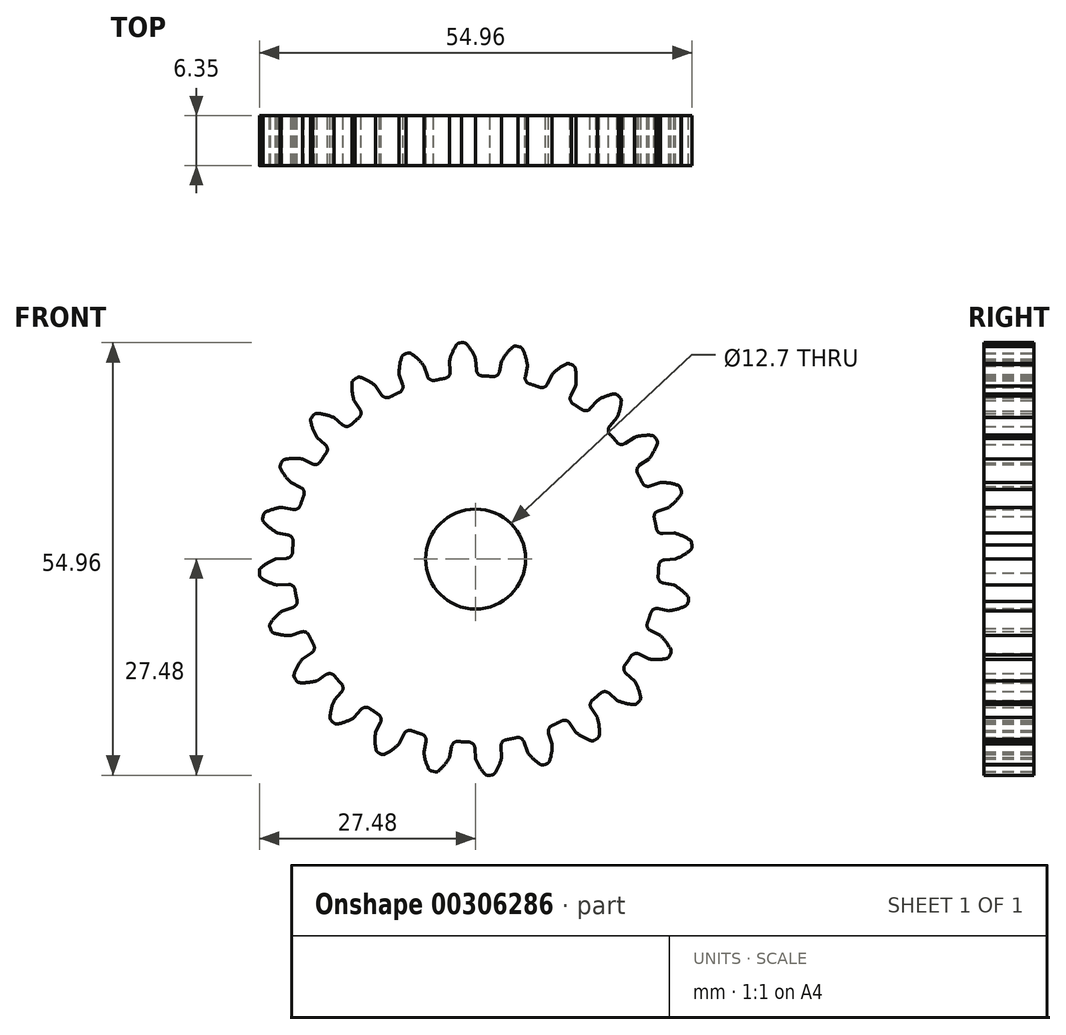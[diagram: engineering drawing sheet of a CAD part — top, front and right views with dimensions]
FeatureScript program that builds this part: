
annotation { "Feature Type Name" : "Feature", "Feature Type Description" : "" }
export const myFeature = defineFeature(function(context is Context, id is Id, definition is map)
    precondition{}
    {
        {
            var Q0;
            Q0=qCreatedBy(makeId("Front.planeOp"),FACE);
            var sketch = newSketch(context, id + "F0", { "sketchPlane" : qUnion([Q0])});
            skArc(sketch, "E0", {"start": v(-3.89, 22.95) * mm, "mid": v(1.52, -23.23) * mm, "end": v(0.86, 23.26) * mm});
            skArc(sketch, "E1.trimOffspring", {"start": v(0, 25.4) * mm, "mid": v(-0.5, 26.4) * mm, "end": v(-1.15, 27.3) * mm});
            skLineSegment(sketch, "E2", {"start": v(0, 25.4) * mm, "end": v(0.1, 24.01) * mm});
            skLineSegment(sketch, "E3", {"start": v(-1.53, 27.48) * mm, "end": v(-1.8, 27.48) * mm});
            skLineSegment(sketch, "E4.MirrorCS", {"start": v(-2.07, 27.44) * mm, "end": v(-1.8, 27.48) * mm});
            skArc(sketch, "E5.MirrorCS", {"start": v(-3.32, 25.18) * mm, "mid": v(-2.96, 26.24) * mm, "end": v(-2.42, 27.22) * mm});
            skLineSegment(sketch, "E6.MirrorCS", {"start": v(-3.32, 25.18) * mm, "end": v(-3.22, 23.8) * mm});
            skPoint(sketch, "E7.visualSharp", {"position": v(-1.3, 27.48) * mm});
            skArc(sketch, "E7.filletArc", {"start": v(-1.15, 27.3) * mm, "mid": v(-1.32, 27.43) * mm, "end": v(-1.53, 27.48) * mm});
            skPoint(sketch, "E8.visualSharp", {"position": v(-2.3, 27.41) * mm});
            skArc(sketch, "E8.filletArc", {"start": v(-2.07, 27.44) * mm, "mid": v(-2.27, 27.37) * mm, "end": v(-2.42, 27.22) * mm});
            skPoint(sketch, "E9.visualSharp", {"position": v(0.14, 23.28) * mm});
            skArc(sketch, "E9.filletArc", {"start": v(0.1, 24.01) * mm, "mid": v(0.33, 23.49) * mm, "end": v(0.86, 23.26) * mm});
            skPoint(sketch, "E10.visualSharp", {"position": v(-3.18, 23.06) * mm});
            skArc(sketch, "E10.filletArc", {"start": v(-3.89, 22.95) * mm, "mid": v(-3.4, 23.24) * mm, "end": v(-3.22, 23.8) * mm});
            skLineSegment(sketch, "E11.1.0", {"start": v(-9.72, 23.47) * mm, "end": v(-9.27, 22.15) * mm});
            skLineSegment(sketch, "E11.1.1", {"start": v(-6.57, 24.53) * mm, "end": v(-6.13, 23.22) * mm});
            skPoint(sketch, "E11.1.2", {"position": v(-8.37, 26.2) * mm});
            skArc(sketch, "E11.1.3", {"start": v(-6.13, 23.22) * mm, "mid": v(-5.76, 22.77) * mm, "end": v(-5.2, 22.7) * mm});
            skArc(sketch, "E11.1.4", {"start": v(-6.57, 24.53) * mm, "mid": v(-7.3, 25.38) * mm, "end": v(-8.18, 26.08) * mm});
            skPoint(sketch, "E11.1.5", {"position": v(-9.3, 25.89) * mm});
            skArc(sketch, "E11.1.6", {"start": v(-9.72, 23.47) * mm, "mid": v(-9.65, 24.58) * mm, "end": v(-9.39, 25.67) * mm});
            skArc(sketch, "E11.1.7", {"start": v(-9.7, 21.16) * mm, "mid": v(-9.3, 21.57) * mm, "end": v(-9.27, 22.15) * mm});
            skLineSegment(sketch, "E11.1.8", {"start": v(-8.6, 26.14) * mm, "end": v(-8.85, 26.07) * mm});
            skArc(sketch, "E11.1.9", {"start": v(-8.18, 26.08) * mm, "mid": v(-8.38, 26.15) * mm, "end": v(-8.6, 26.14) * mm});
            skArc(sketch, "E11.1.10", {"start": v(-9.1, 25.97) * mm, "mid": v(-9.28, 25.85) * mm, "end": v(-9.39, 25.67) * mm});
            skLineSegment(sketch, "E11.1.11", {"start": v(-9.1, 25.97) * mm, "end": v(-8.85, 26.07) * mm});
            skLineSegment(sketch, "E11.2.0", {"start": v(-15.46, 20.15) * mm, "end": v(-14.69, 19) * mm});
            skLineSegment(sketch, "E11.2.1", {"start": v(-12.7, 22) * mm, "end": v(-11.93, 20.84) * mm});
            skPoint(sketch, "E11.2.2", {"position": v(-14.87, 23.14) * mm});
            skArc(sketch, "E11.2.3", {"start": v(-11.93, 20.84) * mm, "mid": v(-11.46, 20.5) * mm, "end": v(-10.89, 20.58) * mm});
            skArc(sketch, "E11.2.4", {"start": v(-12.7, 22) * mm, "mid": v(-13.63, 22.62) * mm, "end": v(-14.65, 23.07) * mm});
            skPoint(sketch, "E11.2.5", {"position": v(-15.7, 22.6) * mm});
            skArc(sketch, "E11.2.6", {"start": v(-15.46, 20.15) * mm, "mid": v(-15.68, 21.25) * mm, "end": v(-15.7, 22.36) * mm});
            skArc(sketch, "E11.2.7", {"start": v(-14.84, 17.93) * mm, "mid": v(-14.56, 18.43) * mm, "end": v(-14.69, 19) * mm});
            skLineSegment(sketch, "E11.2.8", {"start": v(-15.06, 23.03) * mm, "end": v(-15.3, 22.9) * mm});
            skArc(sketch, "E11.2.9", {"start": v(-14.65, 23.07) * mm, "mid": v(-14.86, 23.1) * mm, "end": v(-15.06, 23.03) * mm});
            skArc(sketch, "E11.2.10", {"start": v(-15.51, 22.73) * mm, "mid": v(-15.65, 22.57) * mm, "end": v(-15.7, 22.36) * mm});
            skLineSegment(sketch, "E11.2.11", {"start": v(-15.51, 22.73) * mm, "end": v(-15.3, 22.9) * mm});
            skLineSegment(sketch, "E11.3.0", {"start": v(-20.15, 15.46) * mm, "end": v(-19.1, 14.54) * mm});
            skLineSegment(sketch, "E11.3.1", {"start": v(-17.96, 17.96) * mm, "end": v(-16.91, 17.04) * mm});
            skPoint(sketch, "E11.3.2", {"position": v(-20.35, 18.5) * mm});
            skArc(sketch, "E11.3.3", {"start": v(-16.91, 17.04) * mm, "mid": v(-16.37, 16.84) * mm, "end": v(-15.84, 17.06) * mm});
            skArc(sketch, "E11.3.4", {"start": v(-17.96, 17.96) * mm, "mid": v(-19.02, 18.32) * mm, "end": v(-20.12, 18.5) * mm});
            skPoint(sketch, "E11.3.5", {"position": v(-21, 17.76) * mm});
            skArc(sketch, "E11.3.6", {"start": v(-20.15, 15.46) * mm, "mid": v(-20.65, 16.46) * mm, "end": v(-20.96, 17.53) * mm});
            skArc(sketch, "E11.3.7", {"start": v(-18.98, 13.48) * mm, "mid": v(-18.84, 14.04) * mm, "end": v(-19.1, 14.54) * mm});
            skLineSegment(sketch, "E11.3.8", {"start": v(-20.51, 18.35) * mm, "end": v(-20.7, 18.16) * mm});
            skArc(sketch, "E11.3.9", {"start": v(-20.12, 18.5) * mm, "mid": v(-20.33, 18.46) * mm, "end": v(-20.51, 18.35) * mm});
            skArc(sketch, "E11.3.10", {"start": v(-20.87, 17.94) * mm, "mid": v(-20.96, 17.75) * mm, "end": v(-20.96, 17.53) * mm});
            skLineSegment(sketch, "E11.3.11", {"start": v(-20.87, 17.94) * mm, "end": v(-20.7, 18.16) * mm});
            skLineSegment(sketch, "E11.4.0", {"start": v(-23.47, 9.72) * mm, "end": v(-22.22, 9.1) * mm});
            skLineSegment(sketch, "E11.4.1", {"start": v(-22, 12.7) * mm, "end": v(-20.75, 12.08) * mm});
            skPoint(sketch, "E11.4.2", {"position": v(-24.45, 12.6) * mm});
            skArc(sketch, "E11.4.3", {"start": v(-20.75, 12.08) * mm, "mid": v(-20.18, 12.03) * mm, "end": v(-19.72, 12.38) * mm});
            skArc(sketch, "E11.4.4", {"start": v(-22, 12.7) * mm, "mid": v(-23.11, 12.78) * mm, "end": v(-24.22, 12.66) * mm});
            skPoint(sketch, "E11.4.5", {"position": v(-24.89, 11.72) * mm});
            skArc(sketch, "E11.4.6", {"start": v(-23.47, 9.72) * mm, "mid": v(-24.2, 10.56) * mm, "end": v(-24.79, 11.51) * mm});
            skArc(sketch, "E11.4.7", {"start": v(-21.82, 8.1) * mm, "mid": v(-21.83, 8.68) * mm, "end": v(-22.22, 9.1) * mm});
            skLineSegment(sketch, "E11.4.8", {"start": v(-24.56, 12.41) * mm, "end": v(-24.7, 12.18) * mm});
            skArc(sketch, "E11.4.9", {"start": v(-24.22, 12.66) * mm, "mid": v(-24.42, 12.57) * mm, "end": v(-24.56, 12.41) * mm});
            skArc(sketch, "E11.4.10", {"start": v(-24.8, 11.93) * mm, "mid": v(-24.84, 11.72) * mm, "end": v(-24.79, 11.51) * mm});
            skLineSegment(sketch, "E11.4.11", {"start": v(-24.8, 11.93) * mm, "end": v(-24.7, 12.18) * mm});
            skLineSegment(sketch, "E11.5.0", {"start": v(-25.18, 3.32) * mm, "end": v(-23.82, 3.04) * mm});
            skLineSegment(sketch, "E11.5.1", {"start": v(-24.53, 6.57) * mm, "end": v(-23.17, 6.3) * mm});
            skPoint(sketch, "E11.5.2", {"position": v(-26.88, 5.85) * mm});
            skArc(sketch, "E11.5.3", {"start": v(-23.17, 6.3) * mm, "mid": v(-22.6, 6.4) * mm, "end": v(-22.25, 6.85) * mm});
            skArc(sketch, "E11.5.4", {"start": v(-24.53, 6.57) * mm, "mid": v(-25.63, 6.36) * mm, "end": v(-26.67, 5.96) * mm});
            skPoint(sketch, "E11.5.5", {"position": v(-27.07, 4.88) * mm});
            skArc(sketch, "E11.5.6", {"start": v(-25.18, 3.32) * mm, "mid": v(-26.11, 3.93) * mm, "end": v(-26.92, 4.7) * mm});
            skArc(sketch, "E11.5.7", {"start": v(-23.18, 2.18) * mm, "mid": v(-23.33, 2.74) * mm, "end": v(-23.82, 3.04) * mm});
            skLineSegment(sketch, "E11.5.8", {"start": v(-26.94, 5.63) * mm, "end": v(-27, 5.37) * mm});
            skArc(sketch, "E11.5.9", {"start": v(-26.67, 5.96) * mm, "mid": v(-26.84, 5.82) * mm, "end": v(-26.94, 5.63) * mm});
            skArc(sketch, "E11.5.10", {"start": v(-27.04, 5.1) * mm, "mid": v(-27.02, 4.9) * mm, "end": v(-26.92, 4.7) * mm});
            skLineSegment(sketch, "E11.5.11", {"start": v(-27.04, 5.1) * mm, "end": v(-27, 5.37) * mm});
            skLineSegment(sketch, "E11.6.0", {"start": v(-25.18, -3.32) * mm, "end": v(-23.8, -3.22) * mm});
            skLineSegment(sketch, "E11.6.1", {"start": v(-25.4, 0) * mm, "end": v(-24.01, 0.1) * mm});
            skPoint(sketch, "E11.6.2", {"position": v(-27.48, -1.3) * mm});
            skArc(sketch, "E11.6.3", {"start": v(-24.01, 0.1) * mm, "mid": v(-23.49, 0.33) * mm, "end": v(-23.26, 0.86) * mm});
            skArc(sketch, "E11.6.4", {"start": v(-25.4, 0) * mm, "mid": v(-26.4, -0.5) * mm, "end": v(-27.3, -1.15) * mm});
            skPoint(sketch, "E11.6.5", {"position": v(-27.41, -2.3) * mm});
            skArc(sketch, "E11.6.6", {"start": v(-25.18, -3.32) * mm, "mid": v(-26.24, -2.96) * mm, "end": v(-27.22, -2.42) * mm});
            skArc(sketch, "E11.6.7", {"start": v(-22.95, -3.89) * mm, "mid": v(-23.24, -3.4) * mm, "end": v(-23.8, -3.22) * mm});
            skLineSegment(sketch, "E11.6.8", {"start": v(-27.48, -1.53) * mm, "end": v(-27.48, -1.8) * mm});
            skArc(sketch, "E11.6.9", {"start": v(-27.3, -1.15) * mm, "mid": v(-27.43, -1.32) * mm, "end": v(-27.48, -1.53) * mm});
            skArc(sketch, "E11.6.10", {"start": v(-27.44, -2.07) * mm, "mid": v(-27.37, -2.27) * mm, "end": v(-27.22, -2.42) * mm});
            skLineSegment(sketch, "E11.6.11", {"start": v(-27.44, -2.07) * mm, "end": v(-27.48, -1.8) * mm});
            skLineSegment(sketch, "E11.7.0", {"start": v(-23.47, -9.72) * mm, "end": v(-22.15, -9.27) * mm});
            skLineSegment(sketch, "E11.7.1", {"start": v(-24.53, -6.57) * mm, "end": v(-23.22, -6.13) * mm});
            skPoint(sketch, "E11.7.2", {"position": v(-26.2, -8.37) * mm});
            skArc(sketch, "E11.7.3", {"start": v(-23.22, -6.13) * mm, "mid": v(-22.77, -5.76) * mm, "end": v(-22.7, -5.2) * mm});
            skArc(sketch, "E11.7.4", {"start": v(-24.53, -6.57) * mm, "mid": v(-25.38, -7.3) * mm, "end": v(-26.08, -8.18) * mm});
            skPoint(sketch, "E11.7.5", {"position": v(-25.89, -9.3) * mm});
            skArc(sketch, "E11.7.6", {"start": v(-23.47, -9.72) * mm, "mid": v(-24.58, -9.65) * mm, "end": v(-25.67, -9.39) * mm});
            skArc(sketch, "E11.7.7", {"start": v(-21.16, -9.7) * mm, "mid": v(-21.57, -9.3) * mm, "end": v(-22.15, -9.27) * mm});
            skLineSegment(sketch, "E11.7.8", {"start": v(-26.14, -8.6) * mm, "end": v(-26.07, -8.85) * mm});
            skArc(sketch, "E11.7.9", {"start": v(-26.08, -8.18) * mm, "mid": v(-26.15, -8.38) * mm, "end": v(-26.14, -8.6) * mm});
            skArc(sketch, "E11.7.10", {"start": v(-25.97, -9.1) * mm, "mid": v(-25.85, -9.28) * mm, "end": v(-25.67, -9.39) * mm});
            skLineSegment(sketch, "E11.7.11", {"start": v(-25.97, -9.1) * mm, "end": v(-26.07, -8.85) * mm});
            skLineSegment(sketch, "E11.8.0", {"start": v(-20.15, -15.46) * mm, "end": v(-19, -14.69) * mm});
            skLineSegment(sketch, "E11.8.1", {"start": v(-22, -12.7) * mm, "end": v(-20.84, -11.93) * mm});
            skPoint(sketch, "E11.8.2", {"position": v(-23.14, -14.87) * mm});
            skArc(sketch, "E11.8.3", {"start": v(-20.84, -11.93) * mm, "mid": v(-20.5, -11.46) * mm, "end": v(-20.58, -10.89) * mm});
            skArc(sketch, "E11.8.4", {"start": v(-22, -12.7) * mm, "mid": v(-22.62, -13.63) * mm, "end": v(-23.07, -14.65) * mm});
            skPoint(sketch, "E11.8.5", {"position": v(-22.6, -15.7) * mm});
            skArc(sketch, "E11.8.6", {"start": v(-20.15, -15.46) * mm, "mid": v(-21.25, -15.68) * mm, "end": v(-22.36, -15.7) * mm});
            skArc(sketch, "E11.8.7", {"start": v(-17.93, -14.84) * mm, "mid": v(-18.43, -14.56) * mm, "end": v(-19, -14.69) * mm});
            skLineSegment(sketch, "E11.8.8", {"start": v(-23.03, -15.06) * mm, "end": v(-22.9, -15.3) * mm});
            skArc(sketch, "E11.8.9", {"start": v(-23.07, -14.65) * mm, "mid": v(-23.1, -14.86) * mm, "end": v(-23.03, -15.06) * mm});
            skArc(sketch, "E11.8.10", {"start": v(-22.73, -15.51) * mm, "mid": v(-22.57, -15.65) * mm, "end": v(-22.36, -15.7) * mm});
            skLineSegment(sketch, "E11.8.11", {"start": v(-22.73, -15.51) * mm, "end": v(-22.9, -15.3) * mm});
            skLineSegment(sketch, "E11.9.0", {"start": v(-15.46, -20.15) * mm, "end": v(-14.54, -19.1) * mm});
            skLineSegment(sketch, "E11.9.1", {"start": v(-17.96, -17.96) * mm, "end": v(-17.04, -16.91) * mm});
            skPoint(sketch, "E11.9.2", {"position": v(-18.5, -20.35) * mm});
            skArc(sketch, "E11.9.3", {"start": v(-17.04, -16.91) * mm, "mid": v(-16.84, -16.37) * mm, "end": v(-17.06, -15.84) * mm});
            skArc(sketch, "E11.9.4", {"start": v(-17.96, -17.96) * mm, "mid": v(-18.32, -19.02) * mm, "end": v(-18.5, -20.12) * mm});
            skPoint(sketch, "E11.9.5", {"position": v(-17.76, -21) * mm});
            skArc(sketch, "E11.9.6", {"start": v(-15.46, -20.15) * mm, "mid": v(-16.46, -20.65) * mm, "end": v(-17.53, -20.96) * mm});
            skArc(sketch, "E11.9.7", {"start": v(-13.48, -18.98) * mm, "mid": v(-14.04, -18.84) * mm, "end": v(-14.54, -19.1) * mm});
            skLineSegment(sketch, "E11.9.8", {"start": v(-18.35, -20.51) * mm, "end": v(-18.16, -20.7) * mm});
            skArc(sketch, "E11.9.9", {"start": v(-18.5, -20.12) * mm, "mid": v(-18.46, -20.33) * mm, "end": v(-18.35, -20.51) * mm});
            skArc(sketch, "E11.9.10", {"start": v(-17.94, -20.87) * mm, "mid": v(-17.75, -20.96) * mm, "end": v(-17.53, -20.96) * mm});
            skLineSegment(sketch, "E11.9.11", {"start": v(-17.94, -20.87) * mm, "end": v(-18.16, -20.7) * mm});
            skLineSegment(sketch, "E11.10.0", {"start": v(-9.72, -23.47) * mm, "end": v(-9.1, -22.22) * mm});
            skLineSegment(sketch, "E11.10.1", {"start": v(-12.7, -22) * mm, "end": v(-12.08, -20.75) * mm});
            skPoint(sketch, "E11.10.2", {"position": v(-12.6, -24.45) * mm});
            skArc(sketch, "E11.10.3", {"start": v(-12.08, -20.75) * mm, "mid": v(-12.03, -20.18) * mm, "end": v(-12.38, -19.72) * mm});
            skArc(sketch, "E11.10.4", {"start": v(-12.7, -22) * mm, "mid": v(-12.78, -23.11) * mm, "end": v(-12.66, -24.22) * mm});
            skPoint(sketch, "E11.10.5", {"position": v(-11.72, -24.89) * mm});
            skArc(sketch, "E11.10.6", {"start": v(-9.72, -23.47) * mm, "mid": v(-10.56, -24.2) * mm, "end": v(-11.51, -24.79) * mm});
            skArc(sketch, "E11.10.7", {"start": v(-8.1, -21.82) * mm, "mid": v(-8.68, -21.83) * mm, "end": v(-9.1, -22.22) * mm});
            skLineSegment(sketch, "E11.10.8", {"start": v(-12.41, -24.56) * mm, "end": v(-12.18, -24.7) * mm});
            skArc(sketch, "E11.10.9", {"start": v(-12.66, -24.22) * mm, "mid": v(-12.57, -24.42) * mm, "end": v(-12.41, -24.56) * mm});
            skArc(sketch, "E11.10.10", {"start": v(-11.93, -24.8) * mm, "mid": v(-11.72, -24.84) * mm, "end": v(-11.51, -24.79) * mm});
            skLineSegment(sketch, "E11.10.11", {"start": v(-11.93, -24.8) * mm, "end": v(-12.18, -24.7) * mm});
            skLineSegment(sketch, "E11.11.0", {"start": v(-3.32, -25.18) * mm, "end": v(-3.04, -23.82) * mm});
            skLineSegment(sketch, "E11.11.1", {"start": v(-6.57, -24.53) * mm, "end": v(-6.3, -23.17) * mm});
            skPoint(sketch, "E11.11.2", {"position": v(-5.85, -26.88) * mm});
            skArc(sketch, "E11.11.3", {"start": v(-6.3, -23.17) * mm, "mid": v(-6.4, -22.6) * mm, "end": v(-6.85, -22.25) * mm});
            skArc(sketch, "E11.11.4", {"start": v(-6.57, -24.53) * mm, "mid": v(-6.36, -25.63) * mm, "end": v(-5.96, -26.67) * mm});
            skPoint(sketch, "E11.11.5", {"position": v(-4.88, -27.07) * mm});
            skArc(sketch, "E11.11.6", {"start": v(-3.32, -25.18) * mm, "mid": v(-3.93, -26.11) * mm, "end": v(-4.7, -26.92) * mm});
            skArc(sketch, "E11.11.7", {"start": v(-2.18, -23.18) * mm, "mid": v(-2.74, -23.33) * mm, "end": v(-3.04, -23.82) * mm});
            skLineSegment(sketch, "E11.11.8", {"start": v(-5.63, -26.94) * mm, "end": v(-5.37, -27) * mm});
            skArc(sketch, "E11.11.9", {"start": v(-5.96, -26.67) * mm, "mid": v(-5.82, -26.84) * mm, "end": v(-5.63, -26.94) * mm});
            skArc(sketch, "E11.11.10", {"start": v(-5.1, -27.04) * mm, "mid": v(-4.9, -27.02) * mm, "end": v(-4.7, -26.92) * mm});
            skLineSegment(sketch, "E11.11.11", {"start": v(-5.1, -27.04) * mm, "end": v(-5.37, -27) * mm});
            skLineSegment(sketch, "E11.12.0", {"start": v(3.32, -25.18) * mm, "end": v(3.22, -23.8) * mm});
            skLineSegment(sketch, "E11.12.1", {"start": v(0, -25.4) * mm, "end": v(-0.1, -24.01) * mm});
            skPoint(sketch, "E11.12.2", {"position": v(1.3, -27.48) * mm});
            skArc(sketch, "E11.12.3", {"start": v(-0.1, -24.01) * mm, "mid": v(-0.33, -23.49) * mm, "end": v(-0.86, -23.26) * mm});
            skArc(sketch, "E11.12.4", {"start": v(0, -25.4) * mm, "mid": v(0.5, -26.4) * mm, "end": v(1.15, -27.3) * mm});
            skPoint(sketch, "E11.12.5", {"position": v(2.3, -27.41) * mm});
            skArc(sketch, "E11.12.6", {"start": v(3.32, -25.18) * mm, "mid": v(2.96, -26.24) * mm, "end": v(2.42, -27.22) * mm});
            skArc(sketch, "E11.12.7", {"start": v(3.89, -22.95) * mm, "mid": v(3.4, -23.24) * mm, "end": v(3.22, -23.8) * mm});
            skLineSegment(sketch, "E11.12.8", {"start": v(1.53, -27.48) * mm, "end": v(1.8, -27.48) * mm});
            skArc(sketch, "E11.12.9", {"start": v(1.15, -27.3) * mm, "mid": v(1.32, -27.43) * mm, "end": v(1.53, -27.48) * mm});
            skArc(sketch, "E11.12.10", {"start": v(2.07, -27.44) * mm, "mid": v(2.27, -27.37) * mm, "end": v(2.42, -27.22) * mm});
            skLineSegment(sketch, "E11.12.11", {"start": v(2.07, -27.44) * mm, "end": v(1.8, -27.48) * mm});
            skLineSegment(sketch, "E11.13.0", {"start": v(9.72, -23.47) * mm, "end": v(9.27, -22.15) * mm});
            skLineSegment(sketch, "E11.13.1", {"start": v(6.57, -24.53) * mm, "end": v(6.13, -23.22) * mm});
            skPoint(sketch, "E11.13.2", {"position": v(8.37, -26.2) * mm});
            skArc(sketch, "E11.13.3", {"start": v(6.13, -23.22) * mm, "mid": v(5.76, -22.77) * mm, "end": v(5.2, -22.7) * mm});
            skArc(sketch, "E11.13.4", {"start": v(6.57, -24.53) * mm, "mid": v(7.3, -25.38) * mm, "end": v(8.18, -26.08) * mm});
            skPoint(sketch, "E11.13.5", {"position": v(9.3, -25.89) * mm});
            skArc(sketch, "E11.13.6", {"start": v(9.72, -23.47) * mm, "mid": v(9.65, -24.58) * mm, "end": v(9.39, -25.67) * mm});
            skArc(sketch, "E11.13.7", {"start": v(9.7, -21.16) * mm, "mid": v(9.3, -21.57) * mm, "end": v(9.27, -22.15) * mm});
            skLineSegment(sketch, "E11.13.8", {"start": v(8.6, -26.14) * mm, "end": v(8.85, -26.07) * mm});
            skArc(sketch, "E11.13.9", {"start": v(8.18, -26.08) * mm, "mid": v(8.38, -26.15) * mm, "end": v(8.6, -26.14) * mm});
            skArc(sketch, "E11.13.10", {"start": v(9.1, -25.97) * mm, "mid": v(9.28, -25.85) * mm, "end": v(9.39, -25.67) * mm});
            skLineSegment(sketch, "E11.13.11", {"start": v(9.1, -25.97) * mm, "end": v(8.85, -26.07) * mm});
            skLineSegment(sketch, "E11.14.0", {"start": v(15.46, -20.15) * mm, "end": v(14.69, -19) * mm});
            skLineSegment(sketch, "E11.14.1", {"start": v(12.7, -22) * mm, "end": v(11.93, -20.84) * mm});
            skPoint(sketch, "E11.14.2", {"position": v(14.87, -23.14) * mm});
            skArc(sketch, "E11.14.3", {"start": v(11.93, -20.84) * mm, "mid": v(11.46, -20.5) * mm, "end": v(10.89, -20.58) * mm});
            skArc(sketch, "E11.14.4", {"start": v(12.7, -22) * mm, "mid": v(13.63, -22.62) * mm, "end": v(14.65, -23.07) * mm});
            skPoint(sketch, "E11.14.5", {"position": v(15.7, -22.6) * mm});
            skArc(sketch, "E11.14.6", {"start": v(15.46, -20.15) * mm, "mid": v(15.68, -21.25) * mm, "end": v(15.7, -22.36) * mm});
            skArc(sketch, "E11.14.7", {"start": v(14.84, -17.93) * mm, "mid": v(14.56, -18.43) * mm, "end": v(14.69, -19) * mm});
            skLineSegment(sketch, "E11.14.8", {"start": v(15.06, -23.03) * mm, "end": v(15.3, -22.9) * mm});
            skArc(sketch, "E11.14.9", {"start": v(14.65, -23.07) * mm, "mid": v(14.86, -23.1) * mm, "end": v(15.06, -23.03) * mm});
            skArc(sketch, "E11.14.10", {"start": v(15.51, -22.73) * mm, "mid": v(15.65, -22.57) * mm, "end": v(15.7, -22.36) * mm});
            skLineSegment(sketch, "E11.14.11", {"start": v(15.51, -22.73) * mm, "end": v(15.3, -22.9) * mm});
            skLineSegment(sketch, "E11.15.0", {"start": v(20.15, -15.46) * mm, "end": v(19.1, -14.54) * mm});
            skLineSegment(sketch, "E11.15.1", {"start": v(17.96, -17.96) * mm, "end": v(16.91, -17.04) * mm});
            skPoint(sketch, "E11.15.2", {"position": v(20.35, -18.5) * mm});
            skArc(sketch, "E11.15.3", {"start": v(16.91, -17.04) * mm, "mid": v(16.37, -16.84) * mm, "end": v(15.84, -17.06) * mm});
            skArc(sketch, "E11.15.4", {"start": v(17.96, -17.96) * mm, "mid": v(19.02, -18.32) * mm, "end": v(20.12, -18.5) * mm});
            skPoint(sketch, "E11.15.5", {"position": v(21, -17.76) * mm});
            skArc(sketch, "E11.15.6", {"start": v(20.15, -15.46) * mm, "mid": v(20.65, -16.46) * mm, "end": v(20.96, -17.53) * mm});
            skArc(sketch, "E11.15.7", {"start": v(18.98, -13.48) * mm, "mid": v(18.84, -14.04) * mm, "end": v(19.1, -14.54) * mm});
            skLineSegment(sketch, "E11.15.8", {"start": v(20.51, -18.35) * mm, "end": v(20.7, -18.16) * mm});
            skArc(sketch, "E11.15.9", {"start": v(20.12, -18.5) * mm, "mid": v(20.33, -18.46) * mm, "end": v(20.51, -18.35) * mm});
            skArc(sketch, "E11.15.10", {"start": v(20.87, -17.94) * mm, "mid": v(20.96, -17.75) * mm, "end": v(20.96, -17.53) * mm});
            skLineSegment(sketch, "E11.15.11", {"start": v(20.87, -17.94) * mm, "end": v(20.7, -18.16) * mm});
            skLineSegment(sketch, "E11.16.0", {"start": v(23.47, -9.72) * mm, "end": v(22.22, -9.1) * mm});
            skLineSegment(sketch, "E11.16.1", {"start": v(22, -12.7) * mm, "end": v(20.75, -12.08) * mm});
            skPoint(sketch, "E11.16.2", {"position": v(24.45, -12.6) * mm});
            skArc(sketch, "E11.16.3", {"start": v(20.75, -12.08) * mm, "mid": v(20.18, -12.03) * mm, "end": v(19.72, -12.38) * mm});
            skArc(sketch, "E11.16.4", {"start": v(22, -12.7) * mm, "mid": v(23.11, -12.78) * mm, "end": v(24.22, -12.66) * mm});
            skPoint(sketch, "E11.16.5", {"position": v(24.89, -11.72) * mm});
            skArc(sketch, "E11.16.6", {"start": v(23.47, -9.72) * mm, "mid": v(24.2, -10.56) * mm, "end": v(24.79, -11.51) * mm});
            skArc(sketch, "E11.16.7", {"start": v(21.82, -8.1) * mm, "mid": v(21.83, -8.68) * mm, "end": v(22.22, -9.1) * mm});
            skLineSegment(sketch, "E11.16.8", {"start": v(24.56, -12.41) * mm, "end": v(24.7, -12.18) * mm});
            skArc(sketch, "E11.16.9", {"start": v(24.22, -12.66) * mm, "mid": v(24.42, -12.57) * mm, "end": v(24.56, -12.41) * mm});
            skArc(sketch, "E11.16.10", {"start": v(24.8, -11.93) * mm, "mid": v(24.84, -11.72) * mm, "end": v(24.79, -11.51) * mm});
            skLineSegment(sketch, "E11.16.11", {"start": v(24.8, -11.93) * mm, "end": v(24.7, -12.18) * mm});
            skLineSegment(sketch, "E11.17.0", {"start": v(25.18, -3.32) * mm, "end": v(23.82, -3.04) * mm});
            skLineSegment(sketch, "E11.17.1", {"start": v(24.53, -6.57) * mm, "end": v(23.17, -6.3) * mm});
            skPoint(sketch, "E11.17.2", {"position": v(26.88, -5.85) * mm});
            skArc(sketch, "E11.17.3", {"start": v(23.17, -6.3) * mm, "mid": v(22.6, -6.4) * mm, "end": v(22.25, -6.85) * mm});
            skArc(sketch, "E11.17.4", {"start": v(24.53, -6.57) * mm, "mid": v(25.63, -6.36) * mm, "end": v(26.67, -5.96) * mm});
            skPoint(sketch, "E11.17.5", {"position": v(27.07, -4.88) * mm});
            skArc(sketch, "E11.17.6", {"start": v(25.18, -3.32) * mm, "mid": v(26.11, -3.93) * mm, "end": v(26.92, -4.7) * mm});
            skArc(sketch, "E11.17.7", {"start": v(23.18, -2.18) * mm, "mid": v(23.33, -2.74) * mm, "end": v(23.82, -3.04) * mm});
            skLineSegment(sketch, "E11.17.8", {"start": v(26.94, -5.63) * mm, "end": v(27, -5.37) * mm});
            skArc(sketch, "E11.17.9", {"start": v(26.67, -5.96) * mm, "mid": v(26.84, -5.82) * mm, "end": v(26.94, -5.63) * mm});
            skArc(sketch, "E11.17.10", {"start": v(27.04, -5.1) * mm, "mid": v(27.02, -4.9) * mm, "end": v(26.92, -4.7) * mm});
            skLineSegment(sketch, "E11.17.11", {"start": v(27.04, -5.1) * mm, "end": v(27, -5.37) * mm});
            skLineSegment(sketch, "E11.18.0", {"start": v(25.18, 3.32) * mm, "end": v(23.8, 3.22) * mm});
            skLineSegment(sketch, "E11.18.1", {"start": v(25.4, 0) * mm, "end": v(24.01, -0.1) * mm});
            skPoint(sketch, "E11.18.2", {"position": v(27.48, 1.3) * mm});
            skArc(sketch, "E11.18.3", {"start": v(24.01, -0.1) * mm, "mid": v(23.49, -0.33) * mm, "end": v(23.26, -0.86) * mm});
            skArc(sketch, "E11.18.4", {"start": v(25.4, 0) * mm, "mid": v(26.4, 0.5) * mm, "end": v(27.3, 1.15) * mm});
            skPoint(sketch, "E11.18.5", {"position": v(27.41, 2.3) * mm});
            skArc(sketch, "E11.18.6", {"start": v(25.18, 3.32) * mm, "mid": v(26.24, 2.96) * mm, "end": v(27.22, 2.42) * mm});
            skArc(sketch, "E11.18.7", {"start": v(22.95, 3.89) * mm, "mid": v(23.24, 3.4) * mm, "end": v(23.8, 3.22) * mm});
            skLineSegment(sketch, "E11.18.8", {"start": v(27.48, 1.53) * mm, "end": v(27.48, 1.8) * mm});
            skArc(sketch, "E11.18.9", {"start": v(27.3, 1.15) * mm, "mid": v(27.43, 1.32) * mm, "end": v(27.48, 1.53) * mm});
            skArc(sketch, "E11.18.10", {"start": v(27.44, 2.07) * mm, "mid": v(27.37, 2.27) * mm, "end": v(27.22, 2.42) * mm});
            skLineSegment(sketch, "E11.18.11", {"start": v(27.44, 2.07) * mm, "end": v(27.48, 1.8) * mm});
            skLineSegment(sketch, "E11.19.0", {"start": v(23.47, 9.72) * mm, "end": v(22.15, 9.27) * mm});
            skLineSegment(sketch, "E11.19.1", {"start": v(24.53, 6.57) * mm, "end": v(23.22, 6.13) * mm});
            skPoint(sketch, "E11.19.2", {"position": v(26.2, 8.37) * mm});
            skArc(sketch, "E11.19.3", {"start": v(23.22, 6.13) * mm, "mid": v(22.77, 5.76) * mm, "end": v(22.7, 5.2) * mm});
            skArc(sketch, "E11.19.4", {"start": v(24.53, 6.57) * mm, "mid": v(25.38, 7.3) * mm, "end": v(26.08, 8.18) * mm});
            skPoint(sketch, "E11.19.5", {"position": v(25.89, 9.3) * mm});
            skArc(sketch, "E11.19.6", {"start": v(23.47, 9.72) * mm, "mid": v(24.58, 9.65) * mm, "end": v(25.67, 9.39) * mm});
            skArc(sketch, "E11.19.7", {"start": v(21.16, 9.7) * mm, "mid": v(21.57, 9.3) * mm, "end": v(22.15, 9.27) * mm});
            skLineSegment(sketch, "E11.19.8", {"start": v(26.14, 8.6) * mm, "end": v(26.07, 8.85) * mm});
            skArc(sketch, "E11.19.9", {"start": v(26.08, 8.18) * mm, "mid": v(26.15, 8.38) * mm, "end": v(26.14, 8.6) * mm});
            skArc(sketch, "E11.19.10", {"start": v(25.97, 9.1) * mm, "mid": v(25.85, 9.28) * mm, "end": v(25.67, 9.39) * mm});
            skLineSegment(sketch, "E11.19.11", {"start": v(25.97, 9.1) * mm, "end": v(26.07, 8.85) * mm});
            skLineSegment(sketch, "E11.20.0", {"start": v(20.15, 15.46) * mm, "end": v(19, 14.69) * mm});
            skLineSegment(sketch, "E11.20.1", {"start": v(22, 12.7) * mm, "end": v(20.84, 11.93) * mm});
            skPoint(sketch, "E11.20.2", {"position": v(23.14, 14.87) * mm});
            skArc(sketch, "E11.20.3", {"start": v(20.84, 11.93) * mm, "mid": v(20.5, 11.46) * mm, "end": v(20.58, 10.89) * mm});
            skArc(sketch, "E11.20.4", {"start": v(22, 12.7) * mm, "mid": v(22.62, 13.63) * mm, "end": v(23.07, 14.65) * mm});
            skPoint(sketch, "E11.20.5", {"position": v(22.6, 15.7) * mm});
            skArc(sketch, "E11.20.6", {"start": v(20.15, 15.46) * mm, "mid": v(21.25, 15.68) * mm, "end": v(22.36, 15.7) * mm});
            skArc(sketch, "E11.20.7", {"start": v(17.93, 14.84) * mm, "mid": v(18.43, 14.56) * mm, "end": v(19, 14.69) * mm});
            skLineSegment(sketch, "E11.20.8", {"start": v(23.03, 15.06) * mm, "end": v(22.9, 15.3) * mm});
            skArc(sketch, "E11.20.9", {"start": v(23.07, 14.65) * mm, "mid": v(23.1, 14.86) * mm, "end": v(23.03, 15.06) * mm});
            skArc(sketch, "E11.20.10", {"start": v(22.73, 15.51) * mm, "mid": v(22.57, 15.65) * mm, "end": v(22.36, 15.7) * mm});
            skLineSegment(sketch, "E11.20.11", {"start": v(22.73, 15.51) * mm, "end": v(22.9, 15.3) * mm});
            skLineSegment(sketch, "E11.21.0", {"start": v(15.46, 20.15) * mm, "end": v(14.54, 19.1) * mm});
            skLineSegment(sketch, "E11.21.1", {"start": v(17.96, 17.96) * mm, "end": v(17.04, 16.91) * mm});
            skPoint(sketch, "E11.21.2", {"position": v(18.5, 20.35) * mm});
            skArc(sketch, "E11.21.3", {"start": v(17.04, 16.91) * mm, "mid": v(16.84, 16.37) * mm, "end": v(17.06, 15.84) * mm});
            skArc(sketch, "E11.21.4", {"start": v(17.96, 17.96) * mm, "mid": v(18.32, 19.02) * mm, "end": v(18.5, 20.12) * mm});
            skPoint(sketch, "E11.21.5", {"position": v(17.76, 21) * mm});
            skArc(sketch, "E11.21.6", {"start": v(15.46, 20.15) * mm, "mid": v(16.46, 20.65) * mm, "end": v(17.53, 20.96) * mm});
            skArc(sketch, "E11.21.7", {"start": v(13.48, 18.98) * mm, "mid": v(14.04, 18.84) * mm, "end": v(14.54, 19.1) * mm});
            skLineSegment(sketch, "E11.21.8", {"start": v(18.35, 20.51) * mm, "end": v(18.16, 20.7) * mm});
            skArc(sketch, "E11.21.9", {"start": v(18.5, 20.12) * mm, "mid": v(18.46, 20.33) * mm, "end": v(18.35, 20.51) * mm});
            skArc(sketch, "E11.21.10", {"start": v(17.94, 20.87) * mm, "mid": v(17.75, 20.96) * mm, "end": v(17.53, 20.96) * mm});
            skLineSegment(sketch, "E11.21.11", {"start": v(17.94, 20.87) * mm, "end": v(18.16, 20.7) * mm});
            skLineSegment(sketch, "E11.22.0", {"start": v(9.72, 23.47) * mm, "end": v(9.1, 22.22) * mm});
            skLineSegment(sketch, "E11.22.1", {"start": v(12.7, 22) * mm, "end": v(12.08, 20.75) * mm});
            skPoint(sketch, "E11.22.2", {"position": v(12.6, 24.45) * mm});
            skArc(sketch, "E11.22.3", {"start": v(12.08, 20.75) * mm, "mid": v(12.03, 20.18) * mm, "end": v(12.38, 19.72) * mm});
            skArc(sketch, "E11.22.4", {"start": v(12.7, 22) * mm, "mid": v(12.78, 23.11) * mm, "end": v(12.66, 24.22) * mm});
            skPoint(sketch, "E11.22.5", {"position": v(11.72, 24.89) * mm});
            skArc(sketch, "E11.22.6", {"start": v(9.72, 23.47) * mm, "mid": v(10.56, 24.2) * mm, "end": v(11.51, 24.79) * mm});
            skArc(sketch, "E11.22.7", {"start": v(8.1, 21.82) * mm, "mid": v(8.68, 21.83) * mm, "end": v(9.1, 22.22) * mm});
            skLineSegment(sketch, "E11.22.8", {"start": v(12.41, 24.56) * mm, "end": v(12.18, 24.7) * mm});
            skArc(sketch, "E11.22.9", {"start": v(12.66, 24.22) * mm, "mid": v(12.57, 24.42) * mm, "end": v(12.41, 24.56) * mm});
            skArc(sketch, "E11.22.10", {"start": v(11.93, 24.8) * mm, "mid": v(11.72, 24.84) * mm, "end": v(11.51, 24.79) * mm});
            skLineSegment(sketch, "E11.22.11", {"start": v(11.93, 24.8) * mm, "end": v(12.18, 24.7) * mm});
            skLineSegment(sketch, "E11.23.0", {"start": v(3.32, 25.18) * mm, "end": v(3.04, 23.82) * mm});
            skLineSegment(sketch, "E11.23.1", {"start": v(6.57, 24.53) * mm, "end": v(6.3, 23.17) * mm});
            skPoint(sketch, "E11.23.2", {"position": v(5.85, 26.88) * mm});
            skArc(sketch, "E11.23.3", {"start": v(6.3, 23.17) * mm, "mid": v(6.4, 22.6) * mm, "end": v(6.85, 22.25) * mm});
            skArc(sketch, "E11.23.4", {"start": v(6.57, 24.53) * mm, "mid": v(6.36, 25.63) * mm, "end": v(5.96, 26.67) * mm});
            skPoint(sketch, "E11.23.5", {"position": v(4.88, 27.07) * mm});
            skArc(sketch, "E11.23.6", {"start": v(3.32, 25.18) * mm, "mid": v(3.93, 26.11) * mm, "end": v(4.7, 26.92) * mm});
            skArc(sketch, "E11.23.7", {"start": v(2.18, 23.18) * mm, "mid": v(2.74, 23.33) * mm, "end": v(3.04, 23.82) * mm});
            skLineSegment(sketch, "E11.23.8", {"start": v(5.63, 26.94) * mm, "end": v(5.37, 27) * mm});
            skArc(sketch, "E11.23.9", {"start": v(5.96, 26.67) * mm, "mid": v(5.82, 26.84) * mm, "end": v(5.63, 26.94) * mm});
            skArc(sketch, "E11.23.10", {"start": v(5.1, 27.04) * mm, "mid": v(4.9, 27.02) * mm, "end": v(4.7, 26.92) * mm});
            skLineSegment(sketch, "E11.23.11", {"start": v(5.1, 27.04) * mm, "end": v(5.37, 27) * mm});
            skSolve(sketch);
        }
        {
            var Q0;
            Q0 = qSketchRegion(id + "F0", true);
            extrude(context, id + "F1", {"entities" : qUnion([Q0]), "depth" : 6.35 * mm});
        }
        {
            var Q0;
            Q0=sQuery(id+"F0.wireOp",VERTEX,"E0.center");
            var Q1;
            Q1=makeQuery(id+"F1.opExtrude","SWEPT_BODY",BODY,{"disambiguationData":[OSD([sQuery(id+"F0.wireOp",EDGE,"E0"),sQuery(id+"F0.wireOp",EDGE,"E1.trimOffspring"),sQuery(id+"F0.wireOp",EDGE,"E2"),sQuery(id+"F0.wireOp",EDGE,"E3"),sQuery(id+"F0.wireOp",EDGE,"E4.MirrorCS"),sQuery(id+"F0.wireOp",EDGE,"E5.MirrorCS"),sQuery(id+"F0.wireOp",EDGE,"E6.MirrorCS"),sQuery(id+"F0.wireOp",EDGE,"E7.filletArc"),sQuery(id+"F0.wireOp",EDGE,"E8.filletArc"),sQuery(id+"F0.wireOp",EDGE,"E9.filletArc"),sQuery(id+"F0.wireOp",EDGE,"E10.filletArc"),sQuery(id+"F0.wireOp",EDGE,"E11.1.0"),sQuery(id+"F0.wireOp",EDGE,"E11.1.1"),sQuery(id+"F0.wireOp",EDGE,"E11.1.3"),sQuery(id+"F0.wireOp",EDGE,"E11.1.4"),sQuery(id+"F0.wireOp",EDGE,"E11.1.6"),sQuery(id+"F0.wireOp",EDGE,"E11.1.7"),sQuery(id+"F0.wireOp",EDGE,"E11.1.8"),sQuery(id+"F0.wireOp",EDGE,"E11.1.9"),sQuery(id+"F0.wireOp",EDGE,"E11.1.10"),sQuery(id+"F0.wireOp",EDGE,"E11.1.11"),sQuery(id+"F0.wireOp",EDGE,"E11.2.0"),sQuery(id+"F0.wireOp",EDGE,"E11.2.1"),sQuery(id+"F0.wireOp",EDGE,"E11.2.3"),sQuery(id+"F0.wireOp",EDGE,"E11.2.4"),sQuery(id+"F0.wireOp",EDGE,"E11.2.6"),sQuery(id+"F0.wireOp",EDGE,"E11.2.7"),sQuery(id+"F0.wireOp",EDGE,"E11.2.8"),sQuery(id+"F0.wireOp",EDGE,"E11.2.9"),sQuery(id+"F0.wireOp",EDGE,"E11.2.10"),sQuery(id+"F0.wireOp",EDGE,"E11.2.11"),sQuery(id+"F0.wireOp",EDGE,"E11.3.0"),sQuery(id+"F0.wireOp",EDGE,"E11.3.1"),sQuery(id+"F0.wireOp",EDGE,"E11.3.3"),sQuery(id+"F0.wireOp",EDGE,"E11.3.4"),sQuery(id+"F0.wireOp",EDGE,"E11.3.6"),sQuery(id+"F0.wireOp",EDGE,"E11.3.7"),sQuery(id+"F0.wireOp",EDGE,"E11.3.8"),sQuery(id+"F0.wireOp",EDGE,"E11.3.9"),sQuery(id+"F0.wireOp",EDGE,"E11.3.10"),sQuery(id+"F0.wireOp",EDGE,"E11.3.11"),sQuery(id+"F0.wireOp",EDGE,"E11.4.0"),sQuery(id+"F0.wireOp",EDGE,"E11.4.1"),sQuery(id+"F0.wireOp",EDGE,"E11.4.3"),sQuery(id+"F0.wireOp",EDGE,"E11.4.4"),sQuery(id+"F0.wireOp",EDGE,"E11.4.6"),sQuery(id+"F0.wireOp",EDGE,"E11.4.7"),sQuery(id+"F0.wireOp",EDGE,"E11.4.8"),sQuery(id+"F0.wireOp",EDGE,"E11.4.9"),sQuery(id+"F0.wireOp",EDGE,"E11.4.10"),sQuery(id+"F0.wireOp",EDGE,"E11.4.11"),sQuery(id+"F0.wireOp",EDGE,"E11.5.0"),sQuery(id+"F0.wireOp",EDGE,"E11.5.1"),sQuery(id+"F0.wireOp",EDGE,"E11.5.3"),sQuery(id+"F0.wireOp",EDGE,"E11.5.4"),sQuery(id+"F0.wireOp",EDGE,"E11.5.6"),sQuery(id+"F0.wireOp",EDGE,"E11.5.7"),sQuery(id+"F0.wireOp",EDGE,"E11.5.8"),sQuery(id+"F0.wireOp",EDGE,"E11.5.9"),sQuery(id+"F0.wireOp",EDGE,"E11.5.10"),sQuery(id+"F0.wireOp",EDGE,"E11.5.11"),sQuery(id+"F0.wireOp",EDGE,"E11.6.0"),sQuery(id+"F0.wireOp",EDGE,"E11.6.1"),sQuery(id+"F0.wireOp",EDGE,"E11.6.3"),sQuery(id+"F0.wireOp",EDGE,"E11.6.4"),sQuery(id+"F0.wireOp",EDGE,"E11.6.6"),sQuery(id+"F0.wireOp",EDGE,"E11.6.7"),sQuery(id+"F0.wireOp",EDGE,"E11.6.8"),sQuery(id+"F0.wireOp",EDGE,"E11.6.9"),sQuery(id+"F0.wireOp",EDGE,"E11.6.10"),sQuery(id+"F0.wireOp",EDGE,"E11.6.11"),sQuery(id+"F0.wireOp",EDGE,"E11.7.0"),sQuery(id+"F0.wireOp",EDGE,"E11.7.1"),sQuery(id+"F0.wireOp",EDGE,"E11.7.3"),sQuery(id+"F0.wireOp",EDGE,"E11.7.4"),sQuery(id+"F0.wireOp",EDGE,"E11.7.6"),sQuery(id+"F0.wireOp",EDGE,"E11.7.7"),sQuery(id+"F0.wireOp",EDGE,"E11.7.8"),sQuery(id+"F0.wireOp",EDGE,"E11.7.9"),sQuery(id+"F0.wireOp",EDGE,"E11.7.10"),sQuery(id+"F0.wireOp",EDGE,"E11.7.11"),sQuery(id+"F0.wireOp",EDGE,"E11.8.0"),sQuery(id+"F0.wireOp",EDGE,"E11.8.1"),sQuery(id+"F0.wireOp",EDGE,"E11.8.3"),sQuery(id+"F0.wireOp",EDGE,"E11.8.4"),sQuery(id+"F0.wireOp",EDGE,"E11.8.6"),sQuery(id+"F0.wireOp",EDGE,"E11.8.7"),sQuery(id+"F0.wireOp",EDGE,"E11.8.8"),sQuery(id+"F0.wireOp",EDGE,"E11.8.9"),sQuery(id+"F0.wireOp",EDGE,"E11.8.10"),sQuery(id+"F0.wireOp",EDGE,"E11.8.11"),sQuery(id+"F0.wireOp",EDGE,"E11.9.0"),sQuery(id+"F0.wireOp",EDGE,"E11.9.1"),sQuery(id+"F0.wireOp",EDGE,"E11.9.3"),sQuery(id+"F0.wireOp",EDGE,"E11.9.4"),sQuery(id+"F0.wireOp",EDGE,"E11.9.6"),sQuery(id+"F0.wireOp",EDGE,"E11.9.7"),sQuery(id+"F0.wireOp",EDGE,"E11.9.8"),sQuery(id+"F0.wireOp",EDGE,"E11.9.9"),sQuery(id+"F0.wireOp",EDGE,"E11.9.10"),sQuery(id+"F0.wireOp",EDGE,"E11.9.11"),sQuery(id+"F0.wireOp",EDGE,"E11.10.0"),sQuery(id+"F0.wireOp",EDGE,"E11.10.1"),sQuery(id+"F0.wireOp",EDGE,"E11.10.3"),sQuery(id+"F0.wireOp",EDGE,"E11.10.4"),sQuery(id+"F0.wireOp",EDGE,"E11.10.6"),sQuery(id+"F0.wireOp",EDGE,"E11.10.7"),sQuery(id+"F0.wireOp",EDGE,"E11.10.8"),sQuery(id+"F0.wireOp",EDGE,"E11.10.9"),sQuery(id+"F0.wireOp",EDGE,"E11.10.10"),sQuery(id+"F0.wireOp",EDGE,"E11.10.11"),sQuery(id+"F0.wireOp",EDGE,"E11.11.0"),sQuery(id+"F0.wireOp",EDGE,"E11.11.1"),sQuery(id+"F0.wireOp",EDGE,"E11.11.3"),sQuery(id+"F0.wireOp",EDGE,"E11.11.4"),sQuery(id+"F0.wireOp",EDGE,"E11.11.6"),sQuery(id+"F0.wireOp",EDGE,"E11.11.7"),sQuery(id+"F0.wireOp",EDGE,"E11.11.8"),sQuery(id+"F0.wireOp",EDGE,"E11.11.9"),sQuery(id+"F0.wireOp",EDGE,"E11.11.10"),sQuery(id+"F0.wireOp",EDGE,"E11.11.11"),sQuery(id+"F0.wireOp",EDGE,"E11.12.0"),sQuery(id+"F0.wireOp",EDGE,"E11.12.1"),sQuery(id+"F0.wireOp",EDGE,"E11.12.3"),sQuery(id+"F0.wireOp",EDGE,"E11.12.4"),sQuery(id+"F0.wireOp",EDGE,"E11.12.6"),sQuery(id+"F0.wireOp",EDGE,"E11.12.7"),sQuery(id+"F0.wireOp",EDGE,"E11.12.8"),sQuery(id+"F0.wireOp",EDGE,"E11.12.9"),sQuery(id+"F0.wireOp",EDGE,"E11.12.10"),sQuery(id+"F0.wireOp",EDGE,"E11.12.11"),sQuery(id+"F0.wireOp",EDGE,"E11.13.0"),sQuery(id+"F0.wireOp",EDGE,"E11.13.1"),sQuery(id+"F0.wireOp",EDGE,"E11.13.3"),sQuery(id+"F0.wireOp",EDGE,"E11.13.4"),sQuery(id+"F0.wireOp",EDGE,"E11.13.6"),sQuery(id+"F0.wireOp",EDGE,"E11.13.7"),sQuery(id+"F0.wireOp",EDGE,"E11.13.8"),sQuery(id+"F0.wireOp",EDGE,"E11.13.9"),sQuery(id+"F0.wireOp",EDGE,"E11.13.10"),sQuery(id+"F0.wireOp",EDGE,"E11.13.11"),sQuery(id+"F0.wireOp",EDGE,"E11.14.0"),sQuery(id+"F0.wireOp",EDGE,"E11.14.1"),sQuery(id+"F0.wireOp",EDGE,"E11.14.3"),sQuery(id+"F0.wireOp",EDGE,"E11.14.4"),sQuery(id+"F0.wireOp",EDGE,"E11.14.6"),sQuery(id+"F0.wireOp",EDGE,"E11.14.7"),sQuery(id+"F0.wireOp",EDGE,"E11.14.8"),sQuery(id+"F0.wireOp",EDGE,"E11.14.9"),sQuery(id+"F0.wireOp",EDGE,"E11.14.10"),sQuery(id+"F0.wireOp",EDGE,"E11.14.11"),sQuery(id+"F0.wireOp",EDGE,"E11.15.0"),sQuery(id+"F0.wireOp",EDGE,"E11.15.1"),sQuery(id+"F0.wireOp",EDGE,"E11.15.3"),sQuery(id+"F0.wireOp",EDGE,"E11.15.4"),sQuery(id+"F0.wireOp",EDGE,"E11.15.6"),sQuery(id+"F0.wireOp",EDGE,"E11.15.7"),sQuery(id+"F0.wireOp",EDGE,"E11.15.8"),sQuery(id+"F0.wireOp",EDGE,"E11.15.9"),sQuery(id+"F0.wireOp",EDGE,"E11.15.10"),sQuery(id+"F0.wireOp",EDGE,"E11.15.11"),sQuery(id+"F0.wireOp",EDGE,"E11.16.0"),sQuery(id+"F0.wireOp",EDGE,"E11.16.1"),sQuery(id+"F0.wireOp",EDGE,"E11.16.3"),sQuery(id+"F0.wireOp",EDGE,"E11.16.4"),sQuery(id+"F0.wireOp",EDGE,"E11.16.6"),sQuery(id+"F0.wireOp",EDGE,"E11.16.7"),sQuery(id+"F0.wireOp",EDGE,"E11.16.8"),sQuery(id+"F0.wireOp",EDGE,"E11.16.9"),sQuery(id+"F0.wireOp",EDGE,"E11.16.10"),sQuery(id+"F0.wireOp",EDGE,"E11.16.11"),sQuery(id+"F0.wireOp",EDGE,"E11.17.0"),sQuery(id+"F0.wireOp",EDGE,"E11.17.1"),sQuery(id+"F0.wireOp",EDGE,"E11.17.3"),sQuery(id+"F0.wireOp",EDGE,"E11.17.4"),sQuery(id+"F0.wireOp",EDGE,"E11.17.6"),sQuery(id+"F0.wireOp",EDGE,"E11.17.7"),sQuery(id+"F0.wireOp",EDGE,"E11.17.8"),sQuery(id+"F0.wireOp",EDGE,"E11.17.9"),sQuery(id+"F0.wireOp",EDGE,"E11.17.10"),sQuery(id+"F0.wireOp",EDGE,"E11.17.11"),sQuery(id+"F0.wireOp",EDGE,"E11.18.0"),sQuery(id+"F0.wireOp",EDGE,"E11.18.1"),sQuery(id+"F0.wireOp",EDGE,"E11.18.3"),sQuery(id+"F0.wireOp",EDGE,"E11.18.4"),sQuery(id+"F0.wireOp",EDGE,"E11.18.6"),sQuery(id+"F0.wireOp",EDGE,"E11.18.7"),sQuery(id+"F0.wireOp",EDGE,"E11.18.8"),sQuery(id+"F0.wireOp",EDGE,"E11.18.9"),sQuery(id+"F0.wireOp",EDGE,"E11.18.10"),sQuery(id+"F0.wireOp",EDGE,"E11.18.11"),sQuery(id+"F0.wireOp",EDGE,"E11.19.0"),sQuery(id+"F0.wireOp",EDGE,"E11.19.1"),sQuery(id+"F0.wireOp",EDGE,"E11.19.3"),sQuery(id+"F0.wireOp",EDGE,"E11.19.4"),sQuery(id+"F0.wireOp",EDGE,"E11.19.6"),sQuery(id+"F0.wireOp",EDGE,"E11.19.7"),sQuery(id+"F0.wireOp",EDGE,"E11.19.8"),sQuery(id+"F0.wireOp",EDGE,"E11.19.9"),sQuery(id+"F0.wireOp",EDGE,"E11.19.10"),sQuery(id+"F0.wireOp",EDGE,"E11.19.11"),sQuery(id+"F0.wireOp",EDGE,"E11.20.0"),sQuery(id+"F0.wireOp",EDGE,"E11.20.1"),sQuery(id+"F0.wireOp",EDGE,"E11.20.3"),sQuery(id+"F0.wireOp",EDGE,"E11.20.4"),sQuery(id+"F0.wireOp",EDGE,"E11.20.6"),sQuery(id+"F0.wireOp",EDGE,"E11.20.7"),sQuery(id+"F0.wireOp",EDGE,"E11.20.8"),sQuery(id+"F0.wireOp",EDGE,"E11.20.9"),sQuery(id+"F0.wireOp",EDGE,"E11.20.10"),sQuery(id+"F0.wireOp",EDGE,"E11.20.11"),sQuery(id+"F0.wireOp",EDGE,"E11.21.0"),sQuery(id+"F0.wireOp",EDGE,"E11.21.1"),sQuery(id+"F0.wireOp",EDGE,"E11.21.3"),sQuery(id+"F0.wireOp",EDGE,"E11.21.4"),sQuery(id+"F0.wireOp",EDGE,"E11.21.6"),sQuery(id+"F0.wireOp",EDGE,"E11.21.7"),sQuery(id+"F0.wireOp",EDGE,"E11.21.8"),sQuery(id+"F0.wireOp",EDGE,"E11.21.9"),sQuery(id+"F0.wireOp",EDGE,"E11.21.10"),sQuery(id+"F0.wireOp",EDGE,"E11.21.11"),sQuery(id+"F0.wireOp",EDGE,"E11.22.0"),sQuery(id+"F0.wireOp",EDGE,"E11.22.1"),sQuery(id+"F0.wireOp",EDGE,"E11.22.3"),sQuery(id+"F0.wireOp",EDGE,"E11.22.4"),sQuery(id+"F0.wireOp",EDGE,"E11.22.6"),sQuery(id+"F0.wireOp",EDGE,"E11.22.7"),sQuery(id+"F0.wireOp",EDGE,"E11.22.8"),sQuery(id+"F0.wireOp",EDGE,"E11.22.9"),sQuery(id+"F0.wireOp",EDGE,"E11.22.10"),sQuery(id+"F0.wireOp",EDGE,"E11.22.11"),sQuery(id+"F0.wireOp",EDGE,"E11.23.0"),sQuery(id+"F0.wireOp",EDGE,"E11.23.1"),sQuery(id+"F0.wireOp",EDGE,"E11.23.3"),sQuery(id+"F0.wireOp",EDGE,"E11.23.4"),sQuery(id+"F0.wireOp",EDGE,"E11.23.6"),sQuery(id+"F0.wireOp",EDGE,"E11.23.7"),sQuery(id+"F0.wireOp",EDGE,"E11.23.8"),sQuery(id+"F0.wireOp",EDGE,"E11.23.9"),sQuery(id+"F0.wireOp",EDGE,"E11.23.10"),sQuery(id+"F0.wireOp",EDGE,"E11.23.11")])]});
            hole(context, id + "F2", {"style" : HoleStyle.SIMPLE, "endStyle" : HoleEndStyle.BLIND, "oppositeDirection" : true, "holeDiameter" : 12.7 * mm, "holeDepth" : 50.8 * mm, "tappedDepth" : 12.7 * mm, "tapClearance" : 3, "locations" : qUnion([Q0]), "scope" : qUnion([Q1])});
        }
    });
